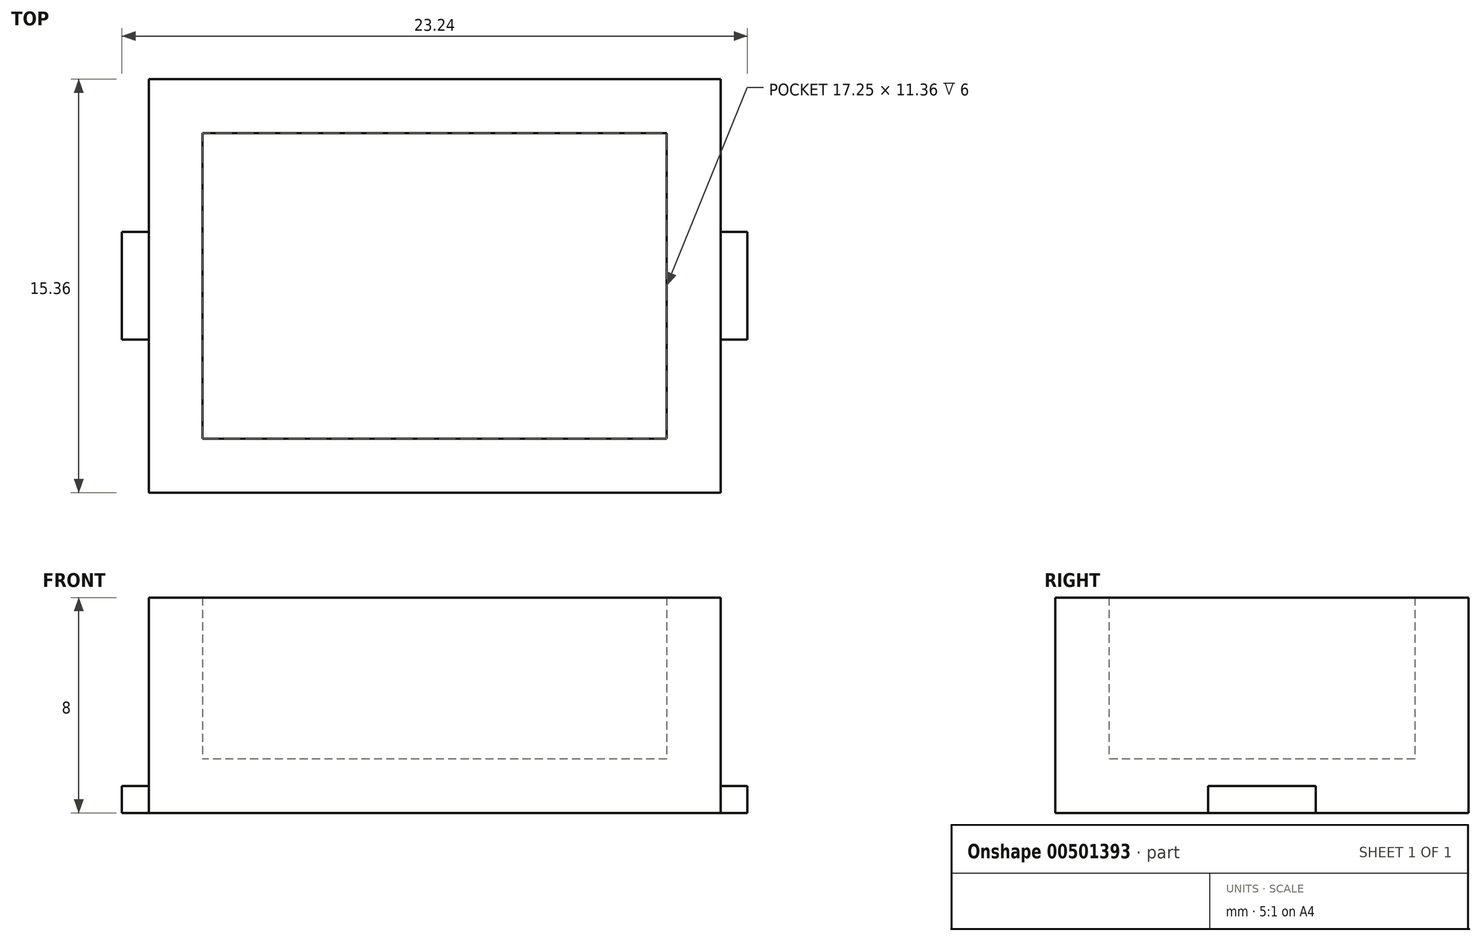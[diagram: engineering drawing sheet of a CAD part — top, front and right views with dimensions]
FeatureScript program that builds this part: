
annotation { "Feature Type Name" : "Feature", "Feature Type Description" : "" }
export const myFeature = defineFeature(function(context is Context, id is Id, definition is map)
    precondition{}
    {
        {
            var Q0;
            Q0=qCreatedBy(makeId("Top.planeOp"),FACE);
            var sketch = newSketch(context, id + "F0", { "sketchPlane" : qUnion([Q0])});
            skLineSegment(sketch, "E0.bottom", {"start": v(10.62, 7.68) * mm, "end": v(-10.62, 7.68) * mm});
            skLineSegment(sketch, "E0.top", {"start": v(10.62, -7.68) * mm, "end": v(-10.62, -7.68) * mm});
            skLineSegment(sketch, "E0.left", {"start": v(10.62, 7.68) * mm, "end": v(10.62, -7.68) * mm});
            skLineSegment(sketch, "E0.right", {"start": v(-10.62, 7.68) * mm, "end": v(-10.62, -7.68) * mm});
            skPoint(sketch, "E0.middle", {"position": v(0, 0) * mm});
            skSolve(sketch);
        }
        {
            var Q0;
            Q0 = qSketchRegion(id + "F0", true);
            extrude(context, id + "F1", {"entities" : qUnion([Q0]), "depth" : 8 * mm});
        }
        {
            var Q0;
            Q0=makeQuery(id+"F1.opExtrude","CAP_FACE",FACE,{"disambiguationData":[OSD([sQuery(id+"F0.wireOp",EDGE,"Amn3bkKI-Sy6c-r9K9-Wdxm-eFbhs8spt4Qz.bottom"),sQuery(id+"F0.wireOp",EDGE,"Amn3bkKI-Sy6c-r9K9-Wdxm-eFbhs8spt4Qz.top"),sQuery(id+"F0.wireOp",EDGE,"Amn3bkKI-Sy6c-r9K9-Wdxm-eFbhs8spt4Qz.left"),sQuery(id+"F0.wireOp",EDGE,"Amn3bkKI-Sy6c-r9K9-Wdxm-eFbhs8spt4Qz.right")])],"isStart":false});
            var Q1;
            Q1=makeQuery(id+"F1.opExtrude","CAP_FACE",FACE,{"disambiguationData":[OSD([sQuery(id+"F0.wireOp",EDGE,"E0.bottom"),sQuery(id+"F0.wireOp",EDGE,"E0.top"),sQuery(id+"F0.wireOp",EDGE,"E0.left"),sQuery(id+"F0.wireOp",EDGE,"E0.right")])],"isStart":false});
            shell(context, id + "F2", {"entities" : qUnion([Q0, Q1]), "thickness" : 2 * mm});
        }
        {
            var Q0;
            Q0=makeQuery(id+"F1.opExtrude","SWEPT_FACE",FACE,{"disambiguationData":[OSD([sQuery(id+"F0.wireOp",EDGE,"E0.right")])]});
            var sketch = newSketch(context, id + "F3", { "sketchPlane" : qUnion([Q0])});
            skLineSegment(sketch, "E1.bottom", {"start": v(2, 1) * mm, "end": v(-2, 1) * mm});
            skPoint(sketch, "E1.middle", {"position": v(0, 0) * mm});
            skLineSegment(sketch, "E2", {"start": v(-2, 0) * mm, "end": v(2, 0) * mm});
            skLineSegment(sketch, "E3", {"start": v(2, 1) * mm, "end": v(2, 0) * mm});
            skLineSegment(sketch, "E4", {"start": v(-2, 1) * mm, "end": v(-2, 0) * mm});
            skSolve(sketch);
        }
        {
            var Q0;
            Q0=makeQuery(id+"F3.imprint","IMPRINT",FACE,{"disambiguationData":[TD([[makeQuery(id+"F3.imprint","IMPRINT",EDGE,{"derivedFrom":sQuery(id+"F3.wireOp",EDGE,"E1.bottom")}),1.0]])]});
            extrude(context, id + "F4", {"entities" : qUnion([Q0]), "operationType" : NewBodyOperationType.ADD, "depth" : 1 * mm});
        }
        {
            var Q0;
            Q0=makeQuery(id+"F1.opExtrude","SWEPT_FACE",FACE,{"disambiguationData":[OSD([sQuery(id+"F0.wireOp",EDGE,"E0.left")])]});
            var sketch = newSketch(context, id + "F5", { "sketchPlane" : qUnion([Q0])});
            skLineSegment(sketch, "E5.bottom", {"start": v(2, 1) * mm, "end": v(-2, 1) * mm});
            skPoint(sketch, "E5.middle", {"position": v(0, 0) * mm});
            skLineSegment(sketch, "E6", {"start": v(-2, 0) * mm, "end": v(2, 0) * mm});
            skLineSegment(sketch, "E7", {"start": v(-2, 1) * mm, "end": v(-2, 0) * mm});
            skLineSegment(sketch, "E8", {"start": v(2, 0) * mm, "end": v(2, 1) * mm});
            skSolve(sketch);
        }
        {
            var Q0;
            Q0 = qSketchRegion(id + "F5", true);
            extrude(context, id + "F6", {"entities" : qUnion([Q0]), "operationType" : NewBodyOperationType.ADD, "depth" : 1 * mm});
        }
    });
